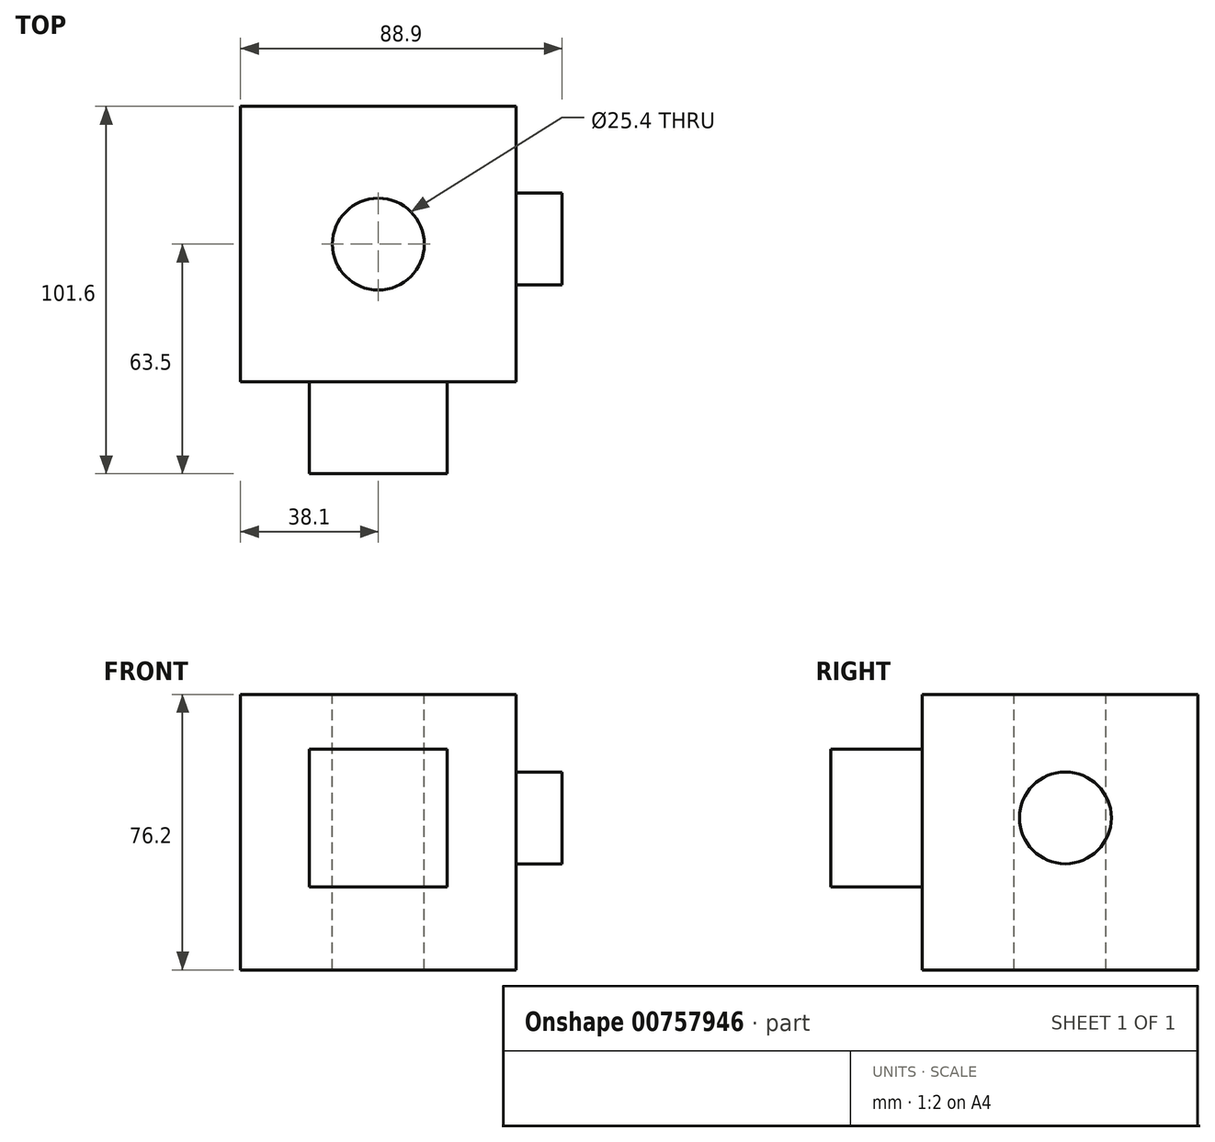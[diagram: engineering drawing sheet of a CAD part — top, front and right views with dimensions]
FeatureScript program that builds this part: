
annotation { "Feature Type Name" : "Feature", "Feature Type Description" : "" }
export const myFeature = defineFeature(function(context is Context, id is Id, definition is map)
    precondition{}
    {
        {
            var Q0;
            Q0=qCreatedBy(makeId("Front.planeOp"),FACE);
            var sketch = newSketch(context, id + "F0", { "sketchPlane" : qUnion([Q0])});
            skLineSegment(sketch, "E0.bottom", {"start": v(38.1, 34.15) * mm, "end": v(-38.1, 34.15) * mm});
            skLineSegment(sketch, "E0.top", {"start": v(38.1, -42.05) * mm, "end": v(-38.1, -42.05) * mm});
            skLineSegment(sketch, "E0.left", {"start": v(38.1, 34.15) * mm, "end": v(38.1, -42.05) * mm});
            skLineSegment(sketch, "E0.right", {"start": v(-38.1, 34.15) * mm, "end": v(-38.1, -42.05) * mm});
            skPoint(sketch, "E0.middle", {"position": v(0, -3.95) * mm});
            skSolve(sketch);
        }
        {
            var Q0;
            Q0 = qSketchRegion(id + "F0", true);
            extrude(context, id + "F1", {"entities" : qUnion([Q0]), "oppositeDirection" : true, "depth" : 76.2 * mm, "offsetDistance" : 25.4 * mm});
        }
        {
            var Q0;
            Q0=makeQuery(id+"F1.opExtrude","SWEPT_FACE",FACE,{"disambiguationData":[OSD([sQuery(id+"F0.wireOp",EDGE,"E0.bottom")])]});
            var sketch = newSketch(context, id + "F2", { "sketchPlane" : qUnion([Q0])});
            skPoint(sketch, "E1", {"position": v(0, 38.1) * mm});
            skSolve(sketch);
        }
        {
            var Q0;
            Q0=sQuery(id+"F2.wireOp",VERTEX,"E1");
            var Q1;
            Q1=makeQuery(id+"F1.opExtrude","SWEPT_BODY",BODY,{"disambiguationData":[OSD([sQuery(id+"F0.wireOp",EDGE,"E0.bottom"),sQuery(id+"F0.wireOp",EDGE,"E0.top"),sQuery(id+"F0.wireOp",EDGE,"E0.left"),sQuery(id+"F0.wireOp",EDGE,"E0.right")])]});
            hole(context, id + "F3", {"style" : HoleStyle.SIMPLE, "endStyle" : HoleEndStyle.THROUGH, "holeDiameter" : 25.4 * mm, "majorDiameter" : 6.35 * mm, "isTappedThrough" : true, "tappedDepth" : 12.7 * mm, "tapClearance" : 3, "locations" : qUnion([Q0]), "scope" : qUnion([Q1])});
        }
        {
            var Q0;
            Q0=makeQuery(id+"F1.opExtrude","CAP_FACE",FACE,{"disambiguationData":[OSD([sQuery(id+"F0.wireOp",EDGE,"E0.bottom"),sQuery(id+"F0.wireOp",EDGE,"E0.top"),sQuery(id+"F0.wireOp",EDGE,"E0.left"),sQuery(id+"F0.wireOp",EDGE,"E0.right")])],"isStart":true});
            var sketch = newSketch(context, id + "F4", { "sketchPlane" : qUnion([Q0])});
            skLineSegment(sketch, "E2.bottom", {"start": v(19.05, -19.05) * mm, "end": v(-19.05, -19.05) * mm});
            skLineSegment(sketch, "E2.top", {"start": v(19.05, 19.05) * mm, "end": v(-19.05, 19.05) * mm});
            skLineSegment(sketch, "E2.left", {"start": v(19.05, -19.05) * mm, "end": v(19.05, 19.05) * mm});
            skLineSegment(sketch, "E2.right", {"start": v(-19.05, -19.05) * mm, "end": v(-19.05, 19.05) * mm});
            skPoint(sketch, "E2.middle", {"position": v(0, 0) * mm});
            skSolve(sketch);
        }
        {
            var Q0;
            Q0=makeQuery(id+"F4.imprint","IMPRINT",FACE,{"disambiguationData":[TD([[makeQuery(id+"F4.imprint","IMPRINT",EDGE,{"derivedFrom":sQuery(id+"F4.wireOp",EDGE,"E2.bottom")}),-1.0]])]});
            extrude(context, id + "F5", {"entities" : qUnion([Q0]), "operationType" : NewBodyOperationType.ADD, "depth" : 25.4 * mm, "offsetDistance" : 25.4 * mm});
        }
        {
            var Q0;
            Q0=makeQuery(id+"F1.opExtrude","SWEPT_FACE",FACE,{"disambiguationData":[OSD([sQuery(id+"F0.wireOp",EDGE,"E0.left")])]});
            var sketch = newSketch(context, id + "F6", { "sketchPlane" : qUnion([Q0])});
            skCircle(sketch, "E3", {"center": v(39.5, 0) * mm, "radius": 12.7 * mm});
            skSolve(sketch);
        }
        {
            var Q0;
            Q0=makeQuery(id+"F6.imprint","IMPRINT",FACE,{"disambiguationData":[TD([[makeQuery(id+"F6.imprint","IMPRINT",EDGE,{"derivedFrom":sQuery(id+"F6.wireOp",EDGE,"E3")}),1.0]])]});
            extrude(context, id + "F7", {"entities" : qUnion([Q0]), "operationType" : NewBodyOperationType.ADD, "depth" : 12.7 * mm, "offsetDistance" : 25.4 * mm});
        }
    });
